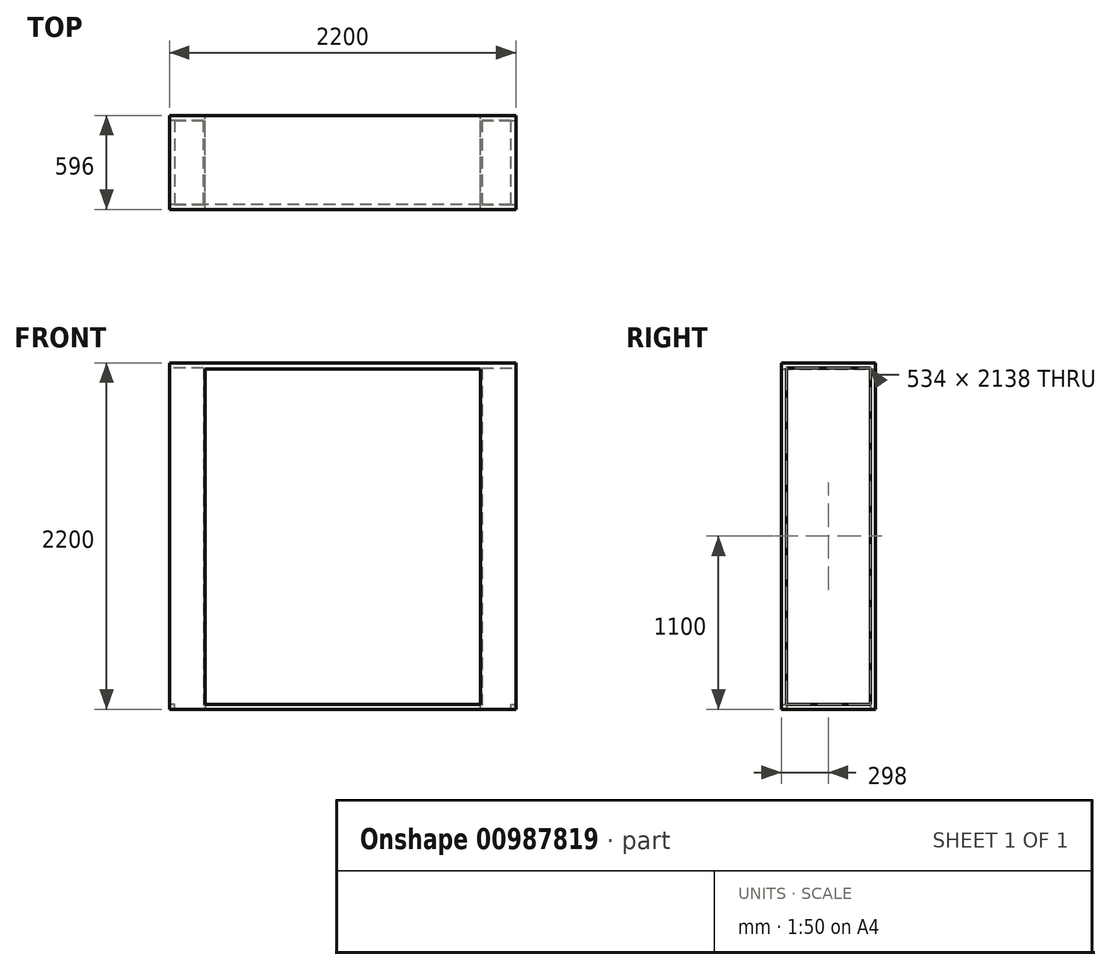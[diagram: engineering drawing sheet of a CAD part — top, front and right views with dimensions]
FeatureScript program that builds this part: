
annotation { "Feature Type Name" : "Feature", "Feature Type Description" : "" }
export const myFeature = defineFeature(function(context is Context, id is Id, definition is map)
    precondition{}
    {
        {
            var Q0;
            Q0=qCreatedBy(makeId("Front.planeOp"),FACE);
            var sketch = newSketch(context, id + "F0", { "sketchPlane" : qUnion([Q0])});
            skLineSegment(sketch, "E0.bottom", {"start": v(-1074.14, 1086.86) * mm, "end": v(1125.86, 1086.86) * mm});
            skLineSegment(sketch, "E0.top", {"start": v(-1074.14, -1113.14) * mm, "end": v(1125.86, -1113.14) * mm});
            skLineSegment(sketch, "E0.left", {"start": v(-1074.14, 1086.86) * mm, "end": v(-1074.14, -1113.14) * mm});
            skLineSegment(sketch, "E0.right", {"start": v(1125.86, 1086.86) * mm, "end": v(1125.86, -1113.14) * mm});
            skSolve(sketch);
        }
        {
            var Q0;
            Q0 = qSketchRegion(id + "F0", true);
            extrude(context, id + "F1", {"entities" : qUnion([Q0]), "oppositeDirection" : true, "depth" : 596 * mm, "offsetDistance" : 25 * mm});
        }
        {
            var Q0;
            Q0=makeQuery(id+"F1.opExtrude","SWEPT_FACE",FACE,{"disambiguationData":[OSD([sQuery(id+"F0.wireOp",EDGE,"E0.bottom")])]});
            var sketch = newSketch(context, id + "F2", { "sketchPlane" : qUnion([Q0])});
            skLineSegment(sketch, "E1.bottom", {"start": v(-848.14, 595) * mm, "end": v(899.86, 595) * mm});
            skLineSegment(sketch, "E1.top", {"start": v(-848.14, 0) * mm, "end": v(899.86, 0) * mm});
            skLineSegment(sketch, "E1.left", {"start": v(-848.14, 595) * mm, "end": v(-848.14, 0) * mm});
            skLineSegment(sketch, "E1.right", {"start": v(899.86, 595) * mm, "end": v(899.86, 0) * mm});
            skSolve(sketch);
        }
        {
            var Q0;
            Q0 = qSketchRegion(id + "F2", true);
            extrude(context, id + "F3", {"entities" : qUnion([Q0]), "operationType" : NewBodyOperationType.REMOVE, "oppositeDirection" : true, "depth" : 2415.5 * mm, "offsetDistance" : 25 * mm});
        }
        {
            var Q0;
            Q0=makeQuery(id+"F3.boolean.opBoolean","COPY",FACE,{"derivedFrom":makeQuery(id+"F3.opExtrude","SWEPT_FACE",FACE,{"disambiguationData":[OSD([sQuery(id+"F2.wireOp",EDGE,"E1.left")])]})});
            var sketch = newSketch(context, id + "F4", { "sketchPlane" : qUnion([Q0])});
            skLineSegment(sketch, "E2.bottom", {"start": v(0, 1086.86) * mm, "end": v(596, 1086.86) * mm});
            skLineSegment(sketch, "E2.top", {"start": v(0, 1048.86) * mm, "end": v(596, 1048.86) * mm});
            skLineSegment(sketch, "E2.left", {"start": v(0, 1086.86) * mm, "end": v(0, 1048.86) * mm});
            skLineSegment(sketch, "E2.right", {"start": v(596, 1086.86) * mm, "end": v(596, 1048.86) * mm});
            skSolve(sketch);
        }
        {
            var Q0;
            Q0 = qSketchRegion(id + "F4", true);
            extrude(context, id + "F5", {"entities" : qUnion([Q0]), "operationType" : NewBodyOperationType.ADD, "depth" : 1753.23 * mm, "offsetDistance" : 25 * mm});
        }
        {
            var Q0;
            Q0=makeQuery(id+"F3.boolean.opBoolean","COPY",FACE,{"derivedFrom":makeQuery(id+"F3.opExtrude","SWEPT_FACE",FACE,{"disambiguationData":[OSD([sQuery(id+"F2.wireOp",EDGE,"E1.left")])]})});
            var sketch = newSketch(context, id + "F6", { "sketchPlane" : qUnion([Q0])});
            skLineSegment(sketch, "E3.bottom", {"start": v(0, -1082.14) * mm, "end": v(31, -1082.14) * mm});
            skLineSegment(sketch, "E3.top", {"start": v(0, -1113.14) * mm, "end": v(31, -1113.14) * mm});
            skLineSegment(sketch, "E3.left", {"start": v(0, -1082.14) * mm, "end": v(0, -1113.14) * mm});
            skLineSegment(sketch, "E3.right", {"start": v(31, -1082.14) * mm, "end": v(31, -1113.14) * mm});
            skSolve(sketch);
        }
        {
            var Q0;
            Q0 = qSketchRegion(id + "F6", true);
            extrude(context, id + "F7", {"entities" : qUnion([Q0]), "operationType" : NewBodyOperationType.ADD, "depth" : 1759.98 * mm, "offsetDistance" : 25 * mm});
        }
        {
            var Q0;
            Q0=makeQuery(id+"F1.opExtrude","SWEPT_FACE",FACE,{"disambiguationData":[OSD([sQuery(id+"F0.wireOp",EDGE,"E0.right")])]});
            var sketch = newSketch(context, id + "F8", { "sketchPlane" : qUnion([Q0])});
            skLineSegment(sketch, "E4.bottom", {"start": v(31, 1055.86) * mm, "end": v(565, 1055.86) * mm});
            skLineSegment(sketch, "E4.top", {"start": v(31, -1082.14) * mm, "end": v(565, -1082.14) * mm});
            skLineSegment(sketch, "E4.left", {"start": v(31, 1055.86) * mm, "end": v(31, -1082.14) * mm});
            skLineSegment(sketch, "E4.right", {"start": v(565, 1055.86) * mm, "end": v(565, -1082.14) * mm});
            skSolve(sketch);
        }
        {
            var Q0;
            Q0 = qSketchRegion(id + "F8", true);
            extrude(context, id + "F9", {"entities" : qUnion([Q0]), "operationType" : NewBodyOperationType.REMOVE, "oppositeDirection" : true, "depth" : 216 * mm, "offsetDistance" : 25 * mm});
        }
        {
            var Q0;
            Q0=makeQuery(id+"F9.boolean.opBoolean","COPY",FACE,{"derivedFrom":makeQuery(id+"F9.opExtrude","SWEPT_FACE",FACE,{"disambiguationData":[OSD([sQuery(id+"F8.wireOp",EDGE,"E4.top")])]})});
            var sketch = newSketch(context, id + "F10", { "sketchPlane" : qUnion([Q0])});
            skLineSegment(sketch, "E5.bottom", {"start": v(1094.86, 31) * mm, "end": v(909.86, 31) * mm});
            skLineSegment(sketch, "E5.top", {"start": v(1094.86, 565) * mm, "end": v(909.86, 565) * mm});
            skLineSegment(sketch, "E5.left", {"start": v(1094.86, 31) * mm, "end": v(1094.86, 565) * mm});
            skLineSegment(sketch, "E5.right", {"start": v(909.86, 31) * mm, "end": v(909.86, 565) * mm});
            skSolve(sketch);
        }
        {
            var Q0;
            Q0 = qSketchRegion(id + "F10", true);
            extrude(context, id + "F11", {"entities" : qUnion([Q0]), "operationType" : NewBodyOperationType.REMOVE, "oppositeDirection" : true, "depth" : 295.37 * mm, "offsetDistance" : 25 * mm});
        }
        {
            var Q0;
            Q0=makeQuery(id+"F1.opExtrude","SWEPT_FACE",FACE,{"disambiguationData":[OSD([sQuery(id+"F0.wireOp",EDGE,"E0.left")])]});
            var sketch = newSketch(context, id + "F12", { "sketchPlane" : qUnion([Q0])});
            skLineSegment(sketch, "E6.bottom", {"start": v(-565, 1055.86) * mm, "end": v(-31, 1055.86) * mm});
            skLineSegment(sketch, "E6.top", {"start": v(-565, -1082.14) * mm, "end": v(-31, -1082.14) * mm});
            skLineSegment(sketch, "E6.left", {"start": v(-565, 1055.86) * mm, "end": v(-565, -1082.14) * mm});
            skLineSegment(sketch, "E6.right", {"start": v(-31, 1055.86) * mm, "end": v(-31, -1082.14) * mm});
            skSolve(sketch);
        }
        {
            var Q0;
            Q0 = qSketchRegion(id + "F12", true);
            extrude(context, id + "F13", {"entities" : qUnion([Q0]), "operationType" : NewBodyOperationType.REMOVE, "oppositeDirection" : true, "depth" : 216 * mm, "offsetDistance" : 25 * mm});
        }
        {
            var Q0;
            Q0=makeQuery(id+"F13.boolean.opBoolean","COPY",FACE,{"derivedFrom":makeQuery(id+"F13.opExtrude","SWEPT_FACE",FACE,{"disambiguationData":[OSD([sQuery(id+"F12.wireOp",EDGE,"E6.top")])]})});
            var sketch = newSketch(context, id + "F14", { "sketchPlane" : qUnion([Q0])});
            skLineSegment(sketch, "E7.bottom", {"start": v(-1043.14, 565) * mm, "end": v(-858.14, 565) * mm});
            skLineSegment(sketch, "E7.top", {"start": v(-1043.14, 31) * mm, "end": v(-858.14, 31) * mm});
            skLineSegment(sketch, "E7.left", {"start": v(-1043.14, 565) * mm, "end": v(-1043.14, 31) * mm});
            skLineSegment(sketch, "E7.right", {"start": v(-858.14, 565) * mm, "end": v(-858.14, 31) * mm});
            skSolve(sketch);
        }
        {
            var Q0;
            Q0 = qSketchRegion(id + "F14", true);
            extrude(context, id + "F15", {"entities" : qUnion([Q0]), "operationType" : NewBodyOperationType.REMOVE, "oppositeDirection" : true, "depth" : 871.48 * mm, "offsetDistance" : 25 * mm});
        }
    });
